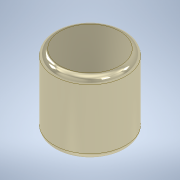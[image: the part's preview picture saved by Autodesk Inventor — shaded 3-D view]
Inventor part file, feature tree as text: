
AUTODESK INVENTOR PART (.ipt)
format: ipt  version: 2022 (Build 260153000, 153)  size: 122,368 bytes
history: native  units: mm
features: extrude x1, fillet x1, sketch x1
ambient origin geometry x8: Origin, YZ Plane, XZ Plane, XY Plane, X Axis, Y Axis, Z Axis, Center Point
bodies: Solid1 (feature_tree)
feature tree (3):
  extrude  "Extrusion1"  Depth=6.0mm TaperAngle=0.0deg
  fillet  "Fillet1"  Radius=0.5mm
  sketch  "Sketch1"  dims[d0=6.0mm d1=6.0mm d2=0.0mm d3=0.5mm]
